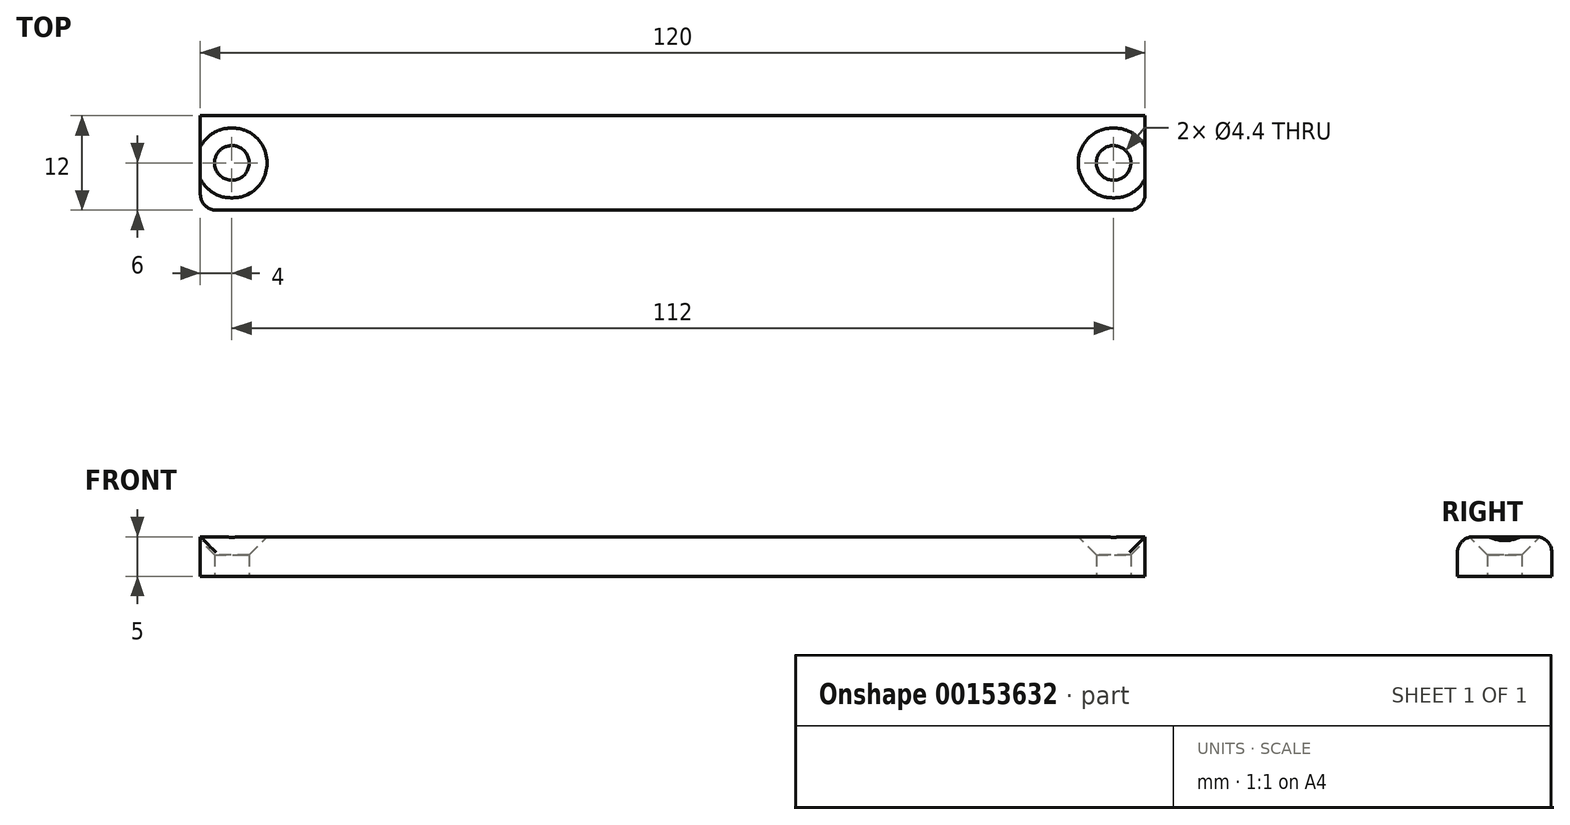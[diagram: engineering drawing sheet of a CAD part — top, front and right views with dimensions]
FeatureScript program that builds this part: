
annotation { "Feature Type Name" : "Feature", "Feature Type Description" : "" }
export const myFeature = defineFeature(function(context is Context, id is Id, definition is map)
    precondition{}
    {
        {
            var Q0;
            Q0=qCreatedBy(makeId("Top.planeOp"),FACE);
            var sketch = newSketch(context, id + "F0", { "sketchPlane" : qUnion([Q0])});
            skLineSegment(sketch, "E0.bottom", {"start": v(0, 0) * mm, "end": v(120, 0) * mm});
            skLineSegment(sketch, "E0.top", {"start": v(0, 12) * mm, "end": v(120, 12) * mm});
            skLineSegment(sketch, "E0.left", {"start": v(0, 0) * mm, "end": v(0, 12) * mm});
            skLineSegment(sketch, "E0.right", {"start": v(120, 0) * mm, "end": v(120, 12) * mm});
            skSolve(sketch);
        }
        {
            var Q0;
            Q0=makeQuery(id+"F0.imprint","IMPRINT",FACE,{"disambiguationData":[TD([[makeQuery(id+"F0.imprint","IMPRINT",EDGE,{"derivedFrom":sQuery(id+"F0.wireOp",EDGE,"E0.bottom")}),1.0]])]});
            extrude(context, id + "F1", {"entities" : qUnion([Q0]), "depth" : 5 * mm});
        }
        {
            var Q0;
            Q0=makeQuery(id+"F1.opExtrude","CAP_FACE",FACE,{"disambiguationData":[OSD([sQuery(id+"F0.wireOp",EDGE,"E0.bottom"),sQuery(id+"F0.wireOp",EDGE,"E0.top"),sQuery(id+"F0.wireOp",EDGE,"E0.left"),sQuery(id+"F0.wireOp",EDGE,"E0.right")])],"isStart":false});
            var sketch = newSketch(context, id + "F2", { "sketchPlane" : qUnion([Q0])});
            skCircle(sketch, "E1", {"center": v(4, 6) * mm, "radius": 1.42 * mm});
            skPoint(sketch, "E1.centerSnap0", {"position": v(0, 6) * mm});
            skCircle(sketch, "E2", {"center": v(116, 6) * mm, "radius": 1.41 * mm});
            skPoint(sketch, "E2.centerSnap0", {"position": v(120, 6) * mm});
            skSolve(sketch);
        }
        {
            var Q0;
            Q0=sQuery(id+"F2.wireOp",VERTEX,"E1.center");
            var Q1;
            Q1=sQuery(id+"F2.wireOp",VERTEX,"E2.center");
            var Q2;
            Q2=makeQuery(id+"F1.opExtrude","SWEPT_BODY",BODY,{"disambiguationData":[OSD([sQuery(id+"F0.wireOp",EDGE,"E0.bottom"),sQuery(id+"F0.wireOp",EDGE,"E0.top"),sQuery(id+"F0.wireOp",EDGE,"E0.left"),sQuery(id+"F0.wireOp",EDGE,"E0.right")])]});
            hole(context, id + "F3", {"style" : HoleStyle.C_SINK, "endStyle" : HoleEndStyle.BLIND, "standardTappedOrClearance" : lookupTablePath({ "standard" : "ISO", "fit" : "Normal", "size" : "M4", "type" : "Clearance" }), "standardBlindInLast" : lookupTablePath({ "fit" : "Standard", "standard" : "ISO", "size" : "M4", "type" : "Clearance" }), "holeDiameter" : 4.4 * mm, "cSinkDiameter" : 8.96 * mm, "cSinkAngle" : 90 * degree, "holeDepth" : 18 * mm, "locations" : qUnion([Q0, Q1]), "scope" : qUnion([Q2])});
        }
        {
            var Q0;
            Q0=makeQuery(id+"F1.opExtrude","CAP_EDGE",EDGE,{"disambiguationData":[OSD([sQuery(id+"F0.wireOp",EDGE,"E0.bottom")])],"isStart":false});
            var Q1;
            Q1=makeQuery(id+"F1.opExtrude","CAP_EDGE",EDGE,{"disambiguationData":[OSD([sQuery(id+"F0.wireOp",EDGE,"E0.top")])],"isStart":false});
            var Q2;
            Q2=makeQuery(id+"F1.opExtrude","SWEPT_EDGE",EDGE,{"disambiguationData":[OSD([sQuery(id+"F0.wireOp",EDGE,"E0.bottom"),sQuery(id+"F0.wireOp",EDGE,"E0.left")])]});
            var Q3;
            Q3=makeQuery(id+"F1.opExtrude","SWEPT_EDGE",EDGE,{"disambiguationData":[OSD([sQuery(id+"F0.wireOp",EDGE,"E0.bottom"),sQuery(id+"F0.wireOp",EDGE,"E0.right")])]});
            fillet(context, id + "F4", {"entities" : qUnion([Q0, Q1, Q2, Q3]), "radius" : 2 * mm, "tangentPropagation" : true, "allowEdgeOverflow" : false});
        }
    });
